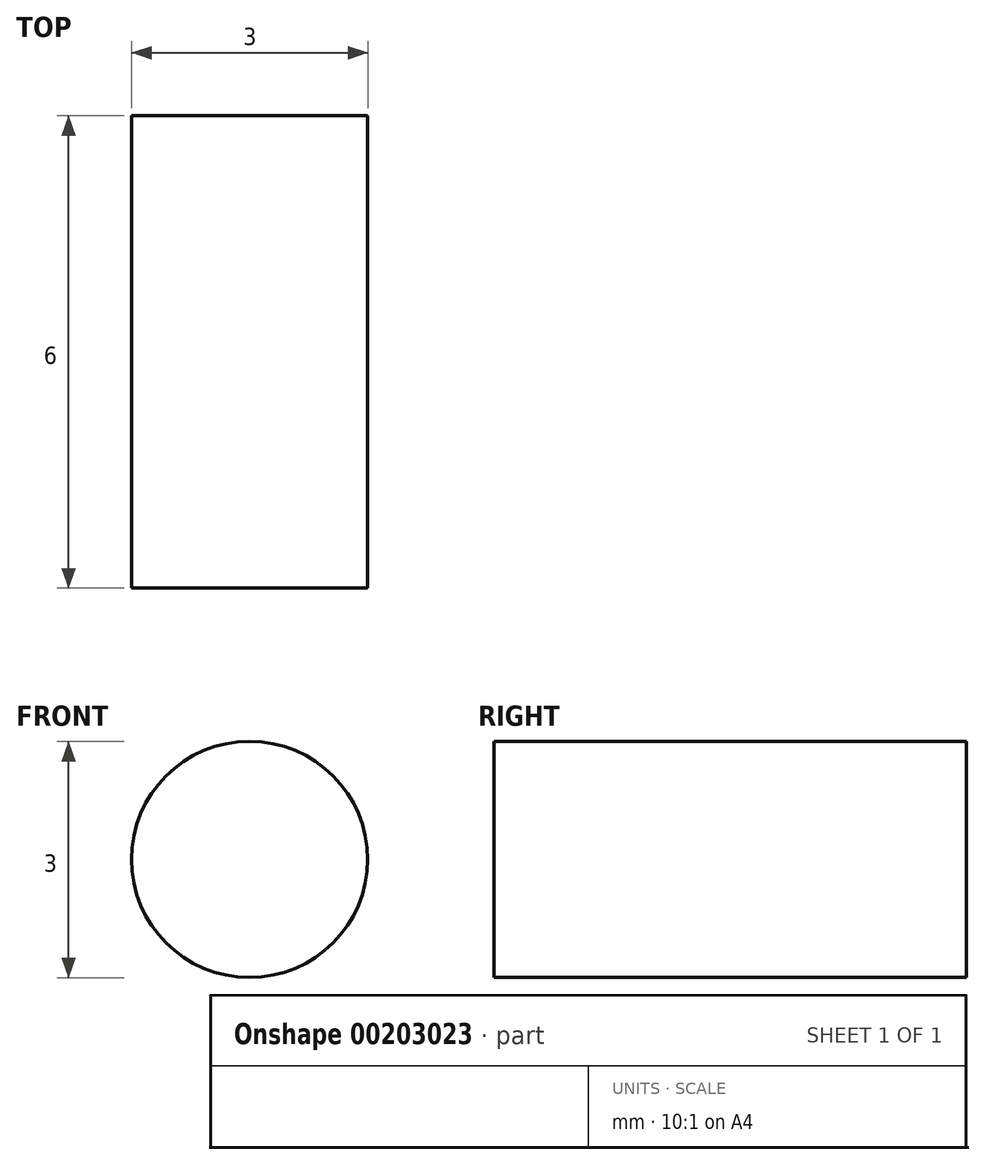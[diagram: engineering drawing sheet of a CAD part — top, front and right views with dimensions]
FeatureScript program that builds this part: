
annotation { "Feature Type Name" : "Feature", "Feature Type Description" : "" }
export const myFeature = defineFeature(function(context is Context, id is Id, definition is map)
    precondition{}
    {
        {
            var Q0;
            Q0=qCreatedBy(makeId("Front.planeOp"),FACE);
            var sketch = newSketch(context, id + "F0", { "sketchPlane" : qUnion([Q0])});
            skCircle(sketch, "E0", {"center": v(110.94, -30.5) * mm, "radius": 1.5 * mm});
            skCircle(sketch, "E1", {"center": v(110.94, 49.1) * mm, "radius": 1.5 * mm});
            skCircle(sketch, "E2", {"center": v(10.94, -30.5) * mm, "radius": 1.5 * mm});
            skCircle(sketch, "E3", {"center": v(10.94, 49.1) * mm, "radius": 1.5 * mm});
            skLineSegment(sketch, "E4", {"start": v(13.94, -37) * mm, "end": v(13.94, -34) * mm});
            skLineSegment(sketch, "E5", {"start": v(13.94, -34) * mm, "end": v(7.94, -34) * mm});
            skLineSegment(sketch, "E6", {"start": v(7.94, -34) * mm, "end": v(7.94, -37) * mm});
            skLineSegment(sketch, "E7", {"start": v(7.94, -37) * mm, "end": v(13.94, -37) * mm});
            skLineSegment(sketch, "E8", {"start": v(13.94, -24) * mm, "end": v(13.94, -27) * mm});
            skLineSegment(sketch, "E9", {"start": v(13.94, -27) * mm, "end": v(7.94, -27) * mm});
            skLineSegment(sketch, "E10", {"start": v(7.94, -27) * mm, "end": v(7.94, -24) * mm});
            skLineSegment(sketch, "E11", {"start": v(7.94, -24) * mm, "end": v(13.94, -24) * mm});
            skLineSegment(sketch, "E12", {"start": v(7.94, 42.6) * mm, "end": v(7.94, 45.6) * mm});
            skLineSegment(sketch, "E13", {"start": v(7.94, 45.6) * mm, "end": v(13.94, 45.6) * mm});
            skLineSegment(sketch, "E14", {"start": v(13.94, 45.6) * mm, "end": v(13.94, 42.6) * mm});
            skLineSegment(sketch, "E15", {"start": v(13.94, 42.6) * mm, "end": v(7.94, 42.6) * mm});
            skLineSegment(sketch, "E16", {"start": v(7.94, 55.6) * mm, "end": v(7.94, 52.6) * mm});
            skLineSegment(sketch, "E17", {"start": v(7.94, 52.6) * mm, "end": v(13.94, 52.6) * mm});
            skLineSegment(sketch, "E18", {"start": v(13.94, 52.6) * mm, "end": v(13.94, 55.6) * mm});
            skLineSegment(sketch, "E19", {"start": v(13.94, 55.6) * mm, "end": v(7.94, 55.6) * mm});
            skLineSegment(sketch, "E20", {"start": v(113.94, 42.6) * mm, "end": v(113.94, 45.6) * mm});
            skLineSegment(sketch, "E21", {"start": v(113.94, 45.6) * mm, "end": v(107.94, 45.6) * mm});
            skLineSegment(sketch, "E22", {"start": v(107.94, 45.6) * mm, "end": v(107.94, 42.6) * mm});
            skLineSegment(sketch, "E23", {"start": v(107.94, 42.6) * mm, "end": v(113.94, 42.6) * mm});
            skLineSegment(sketch, "E24", {"start": v(113.94, 55.6) * mm, "end": v(113.94, 52.6) * mm});
            skLineSegment(sketch, "E25", {"start": v(113.94, 52.6) * mm, "end": v(107.94, 52.6) * mm});
            skLineSegment(sketch, "E26", {"start": v(107.94, 52.6) * mm, "end": v(107.94, 55.6) * mm});
            skLineSegment(sketch, "E27", {"start": v(107.94, 55.6) * mm, "end": v(113.94, 55.6) * mm});
            skLineSegment(sketch, "E28", {"start": v(107.94, -37) * mm, "end": v(107.94, -34) * mm});
            skLineSegment(sketch, "E29", {"start": v(107.94, -34) * mm, "end": v(113.94, -34) * mm});
            skLineSegment(sketch, "E30", {"start": v(113.94, -34) * mm, "end": v(113.94, -37) * mm});
            skLineSegment(sketch, "E31", {"start": v(113.94, -37) * mm, "end": v(107.94, -37) * mm});
            skLineSegment(sketch, "E32", {"start": v(107.94, -24) * mm, "end": v(107.94, -27) * mm});
            skLineSegment(sketch, "E33", {"start": v(107.94, -27) * mm, "end": v(113.94, -27) * mm});
            skLineSegment(sketch, "E34", {"start": v(113.94, -27) * mm, "end": v(113.94, -24) * mm});
            skLineSegment(sketch, "E35", {"start": v(113.94, -24) * mm, "end": v(107.94, -24) * mm});
            skLineSegment(sketch, "E36", {"start": v(83.94, 44.1) * mm, "end": v(83.94, 47.1) * mm});
            skLineSegment(sketch, "E37", {"start": v(83.94, 47.1) * mm, "end": v(77.94, 47.1) * mm});
            skLineSegment(sketch, "E38", {"start": v(77.94, 47.1) * mm, "end": v(77.94, 44.1) * mm});
            skLineSegment(sketch, "E39", {"start": v(77.94, 44.1) * mm, "end": v(83.94, 44.1) * mm});
            skLineSegment(sketch, "E40", {"start": v(37.94, 44.1) * mm, "end": v(37.94, 47.1) * mm});
            skLineSegment(sketch, "E41", {"start": v(37.94, 47.1) * mm, "end": v(43.94, 47.1) * mm});
            skLineSegment(sketch, "E42", {"start": v(43.94, 47.1) * mm, "end": v(43.94, 44.1) * mm});
            skLineSegment(sketch, "E43", {"start": v(43.94, 44.1) * mm, "end": v(37.94, 44.1) * mm});
            skLineSegment(sketch, "E44", {"start": v(30.9, -34.68) * mm, "end": v(29.96, -37.52) * mm});
            skLineSegment(sketch, "E45", {"start": v(29.96, -37.52) * mm, "end": v(35.65, -39.42) * mm});
            skLineSegment(sketch, "E46", {"start": v(35.65, -39.42) * mm, "end": v(36.6, -36.57) * mm});
            skLineSegment(sketch, "E47", {"start": v(36.6, -36.57) * mm, "end": v(30.9, -34.68) * mm});
            skLineSegment(sketch, "E48", {"start": v(90.97, -34.68) * mm, "end": v(91.92, -37.52) * mm});
            skLineSegment(sketch, "E49", {"start": v(91.92, -37.52) * mm, "end": v(86.22, -39.42) * mm});
            skLineSegment(sketch, "E50", {"start": v(86.22, -39.42) * mm, "end": v(85.27, -36.57) * mm});
            skLineSegment(sketch, "E51", {"start": v(85.27, -36.57) * mm, "end": v(90.97, -34.68) * mm});
            skLineSegment(sketch, "E52", {"start": v(57.94, -44.5) * mm, "end": v(57.94, -47.5) * mm});
            skLineSegment(sketch, "E53", {"start": v(57.94, -47.5) * mm, "end": v(63.94, -47.5) * mm});
            skLineSegment(sketch, "E54", {"start": v(63.94, -47.5) * mm, "end": v(63.94, -44.5) * mm});
            skLineSegment(sketch, "E55", {"start": v(63.94, -44.5) * mm, "end": v(57.94, -44.5) * mm});
            skLineSegment(sketch, "E56", {"start": v(83.94, 58.1) * mm, "end": v(83.94, 53.1) * mm});
            skLineSegment(sketch, "E57", {"start": v(83.94, 53.1) * mm, "end": v(80.94, 53.1) * mm});
            skLineSegment(sketch, "E58", {"start": v(80.94, 53.1) * mm, "end": v(77.94, 53.1) * mm});
            skLineSegment(sketch, "E59", {"start": v(77.94, 53.1) * mm, "end": v(77.94, 58.1) * mm});
            skLineSegment(sketch, "E60", {"start": v(77.94, 58.1) * mm, "end": v(76.94, 59.1) * mm});
            skLineSegment(sketch, "E61", {"start": v(76.94, 59.1) * mm, "end": v(44.94, 59.1) * mm});
            skLineSegment(sketch, "E62", {"start": v(44.94, 59.1) * mm, "end": v(43.94, 58.1) * mm});
            skLineSegment(sketch, "E63", {"start": v(43.94, 58.1) * mm, "end": v(43.94, 53.1) * mm});
            skLineSegment(sketch, "E64", {"start": v(43.94, 53.1) * mm, "end": v(40.94, 53.1) * mm});
            skLineSegment(sketch, "E65", {"start": v(40.94, 53.1) * mm, "end": v(37.94, 53.1) * mm});
            skLineSegment(sketch, "E66", {"start": v(37.94, 53.1) * mm, "end": v(37.94, 58.1) * mm});
            skLineSegment(sketch, "E67", {"start": v(37.94, 58.1) * mm, "end": v(36.94, 59.1) * mm});
            skLineSegment(sketch, "E68", {"start": v(36.94, 59.1) * mm, "end": v(5.94, 59.1) * mm});
            skArc(sketch, "E69", {"start": v(5.94, 59.1) * mm, "mid": v(2.4, 57.65) * mm, "end": v(0.94, 54.1) * mm});
            skLineSegment(sketch, "E70", {"start": v(0.94, 54.1) * mm, "end": v(0.94, -36.9) * mm});
            skArc(sketch, "E71", {"start": v(0.94, -36.9) * mm, "mid": v(1.88, -39.82) * mm, "end": v(4.36, -41.64) * mm});
            skLineSegment(sketch, "E72", {"start": v(4.36, -41.64) * mm, "end": v(25.22, -48.59) * mm});
            skLineSegment(sketch, "E73", {"start": v(25.22, -48.59) * mm, "end": v(26.48, -47.96) * mm});
            skLineSegment(sketch, "E74", {"start": v(26.48, -47.96) * mm, "end": v(28.06, -43.21) * mm});
            skLineSegment(sketch, "E75", {"start": v(28.06, -43.21) * mm, "end": v(30.9, -44.16) * mm});
            skLineSegment(sketch, "E76", {"start": v(30.9, -44.16) * mm, "end": v(33.75, -45.11) * mm});
            skLineSegment(sketch, "E77", {"start": v(33.75, -45.11) * mm, "end": v(32.17, -49.85) * mm});
            skLineSegment(sketch, "E78", {"start": v(32.17, -49.85) * mm, "end": v(32.8, -51.12) * mm});
            skLineSegment(sketch, "E79", {"start": v(32.8, -51.12) * mm, "end": v(56.62, -59.06) * mm});
            skArc(sketch, "E80", {"start": v(56.62, -59.06) * mm, "mid": v(57.52, -58.92) * mm, "end": v(57.94, -58.1) * mm});
            skLineSegment(sketch, "E81", {"start": v(57.94, -58.1) * mm, "end": v(57.94, -53.5) * mm});
            skLineSegment(sketch, "E82", {"start": v(57.94, -53.5) * mm, "end": v(60.94, -53.5) * mm});
            skLineSegment(sketch, "E83", {"start": v(60.94, -53.5) * mm, "end": v(63.94, -53.5) * mm});
            skLineSegment(sketch, "E84", {"start": v(63.94, -53.5) * mm, "end": v(63.94, -58.1) * mm});
            skArc(sketch, "E85", {"start": v(63.94, -58.1) * mm, "mid": v(64.35, -58.92) * mm, "end": v(65.25, -59.06) * mm});
            skLineSegment(sketch, "E86", {"start": v(65.25, -59.06) * mm, "end": v(89.07, -51.12) * mm});
            skLineSegment(sketch, "E87", {"start": v(89.07, -51.12) * mm, "end": v(89.7, -49.85) * mm});
            skLineSegment(sketch, "E88", {"start": v(89.7, -49.85) * mm, "end": v(88.12, -45.11) * mm});
            skLineSegment(sketch, "E89", {"start": v(88.12, -45.11) * mm, "end": v(90.97, -44.16) * mm});
            skLineSegment(sketch, "E90", {"start": v(90.97, -44.16) * mm, "end": v(93.81, -43.21) * mm});
            skLineSegment(sketch, "E91", {"start": v(93.81, -43.21) * mm, "end": v(95.4, -47.96) * mm});
            skLineSegment(sketch, "E92", {"start": v(95.4, -47.96) * mm, "end": v(96.66, -48.59) * mm});
            skLineSegment(sketch, "E93", {"start": v(96.66, -48.59) * mm, "end": v(117.52, -41.64) * mm});
            skArc(sketch, "E94", {"start": v(117.52, -41.64) * mm, "mid": v(120, -39.82) * mm, "end": v(120.94, -36.9) * mm});
            skLineSegment(sketch, "E95", {"start": v(120.94, -36.9) * mm, "end": v(120.94, 54.1) * mm});
            skArc(sketch, "E96", {"start": v(120.94, 54.1) * mm, "mid": v(119.47, 57.65) * mm, "end": v(115.94, 59.1) * mm});
            skLineSegment(sketch, "E97", {"start": v(115.94, 59.1) * mm, "end": v(84.94, 59.1) * mm});
            skLineSegment(sketch, "E98", {"start": v(84.94, 59.1) * mm, "end": v(83.94, 58.1) * mm});
            skLineSegment(sketch, "E99", {"start": v(33.68, 31.5) * mm, "end": v(33.68, 37.5) * mm});
            skLineSegment(sketch, "E100", {"start": v(33.68, 37.5) * mm, "end": v(38.68, 37.5) * mm});
            skLineSegment(sketch, "E101", {"start": v(38.68, 37.5) * mm, "end": v(38.68, 31.5) * mm});
            skLineSegment(sketch, "E102", {"start": v(38.68, 31.5) * mm, "end": v(33.68, 31.5) * mm});
            skCircle(sketch, "E103", {"center": v(20.94, -20.5) * mm, "radius": 1.6 * mm});
            skCircle(sketch, "E104", {"center": v(30.94, -20.5) * mm, "radius": 1.6 * mm});
            skCircle(sketch, "E105", {"center": v(90.94, -20.5) * mm, "radius": 1.6 * mm});
            skCircle(sketch, "E106", {"center": v(100.94, -20.5) * mm, "radius": 1.6 * mm});
            skCircle(sketch, "E107", {"center": v(20.94, -10.5) * mm, "radius": 1.6 * mm});
            skCircle(sketch, "E108", {"center": v(30.94, -10.5) * mm, "radius": 1.6 * mm});
            skCircle(sketch, "E109", {"center": v(90.94, -10.5) * mm, "radius": 1.6 * mm});
            skCircle(sketch, "E110", {"center": v(100.94, -10.5) * mm, "radius": 1.6 * mm});
            skCircle(sketch, "E111", {"center": v(20.94, 29.5) * mm, "radius": 1.6 * mm});
            skCircle(sketch, "E112", {"center": v(30.94, 29.5) * mm, "radius": 1.6 * mm});
            skCircle(sketch, "E113", {"center": v(40.94, 29.5) * mm, "radius": 1.6 * mm});
            skCircle(sketch, "E114", {"center": v(50.94, 29.5) * mm, "radius": 1.6 * mm});
            skCircle(sketch, "E115", {"center": v(60.94, 29.5) * mm, "radius": 1.6 * mm});
            skCircle(sketch, "E116", {"center": v(70.94, 29.5) * mm, "radius": 1.6 * mm});
            skCircle(sketch, "E117", {"center": v(80.94, 29.5) * mm, "radius": 1.6 * mm});
            skCircle(sketch, "E118", {"center": v(90.94, 29.5) * mm, "radius": 1.6 * mm});
            skCircle(sketch, "E119", {"center": v(100.94, 29.5) * mm, "radius": 1.6 * mm});
            skCircle(sketch, "E120", {"center": v(20.94, 39.5) * mm, "radius": 1.6 * mm});
            skCircle(sketch, "E121", {"center": v(30.94, 39.5) * mm, "radius": 1.6 * mm});
            skCircle(sketch, "E122", {"center": v(40.94, 39.5) * mm, "radius": 1.6 * mm});
            skCircle(sketch, "E123", {"center": v(50.94, 39.5) * mm, "radius": 1.6 * mm});
            skCircle(sketch, "E124", {"center": v(60.94, 39.5) * mm, "radius": 1.6 * mm});
            skCircle(sketch, "E125", {"center": v(70.94, 39.5) * mm, "radius": 1.6 * mm});
            skCircle(sketch, "E126", {"center": v(80.94, 39.5) * mm, "radius": 1.6 * mm});
            skCircle(sketch, "E127", {"center": v(90.94, 39.5) * mm, "radius": 1.6 * mm});
            skCircle(sketch, "E128", {"center": v(100.94, 39.5) * mm, "radius": 1.6 * mm});
            skCircle(sketch, "E129", {"center": v(70.94, -20.5) * mm, "radius": 1.6 * mm});
            skCircle(sketch, "E130", {"center": v(60.94, -20.5) * mm, "radius": 1.6 * mm});
            skCircle(sketch, "E131", {"center": v(50.94, -20.5) * mm, "radius": 1.6 * mm});
            skLineSegment(sketch, "E132", {"start": v(83.2, 31.5) * mm, "end": v(83.2, 37.5) * mm});
            skLineSegment(sketch, "E133", {"start": v(83.2, 37.5) * mm, "end": v(88.2, 37.5) * mm});
            skLineSegment(sketch, "E134", {"start": v(88.2, 37.5) * mm, "end": v(88.2, 31.5) * mm});
            skLineSegment(sketch, "E135", {"start": v(88.2, 31.5) * mm, "end": v(83.2, 31.5) * mm});
            skLineSegment(sketch, "E136", {"start": v(20.94, 3) * mm, "end": v(20.94, 16) * mm});
            skArc(sketch, "E137", {"start": v(20.94, 16) * mm, "mid": v(22.4, 19.54) * mm, "end": v(25.94, 21) * mm});
            skLineSegment(sketch, "E138", {"start": v(25.94, 21) * mm, "end": v(95.94, 21) * mm});
            skArc(sketch, "E139", {"start": v(95.94, 21) * mm, "mid": v(99.47, 19.54) * mm, "end": v(100.94, 16) * mm});
            skLineSegment(sketch, "E140", {"start": v(100.94, 16) * mm, "end": v(100.94, 3) * mm});
            skArc(sketch, "E141", {"start": v(100.94, 3) * mm, "mid": v(99.47, -0.53) * mm, "end": v(95.94, -2) * mm});
            skLineSegment(sketch, "E142", {"start": v(95.94, -2) * mm, "end": v(25.94, -2) * mm});
            skArc(sketch, "E143", {"start": v(25.94, -2) * mm, "mid": v(22.4, -0.53) * mm, "end": v(20.94, 3) * mm});
            skCircle(sketch, "E144", {"center": v(40.94, -10.5) * mm, "radius": 1.6 * mm});
            skCircle(sketch, "E145", {"center": v(50.94, -10.5) * mm, "radius": 1.6 * mm});
            skCircle(sketch, "E146", {"center": v(60.94, -10.5) * mm, "radius": 1.6 * mm});
            skCircle(sketch, "E147", {"center": v(70.94, -10.5) * mm, "radius": 1.6 * mm});
            skCircle(sketch, "E148", {"center": v(80.94, -20.5) * mm, "radius": 1.6 * mm});
            skCircle(sketch, "E149", {"center": v(80.94, -10.5) * mm, "radius": 1.6 * mm});
            skCircle(sketch, "E150", {"center": v(40.94, -20.5) * mm, "radius": 1.6 * mm});
            skCircle(sketch, "E151", {"center": v(70.94, -30.5) * mm, "radius": 1.6 * mm});
            skCircle(sketch, "E152", {"center": v(60.94, -30.5) * mm, "radius": 1.6 * mm});
            skCircle(sketch, "E153", {"center": v(50.94, -30.5) * mm, "radius": 1.6 * mm});
            skCircle(sketch, "E154", {"center": v(80.94, -30.5) * mm, "radius": 1.6 * mm});
            skCircle(sketch, "E155", {"center": v(40.94, -30.5) * mm, "radius": 1.6 * mm});
            skCircle(sketch, "E156", {"center": v(70.94, -40.5) * mm, "radius": 1.6 * mm});
            skCircle(sketch, "E157", {"center": v(60.94, -40.5) * mm, "radius": 1.6 * mm});
            skCircle(sketch, "E158", {"center": v(50.94, -40.5) * mm, "radius": 1.6 * mm});
            skSolve(sketch);
        }
        {
            var Q0;
            Q0=makeQuery(id+"F0.imprint","IMPRINT",FACE,{"disambiguationData":[TD([[makeQuery(id+"F0.imprint","IMPRINT",EDGE,{"derivedFrom":sQuery(id+"F0.wireOp",EDGE,"E0")}),1.0]])]});
            extrude(context, id + "F1", {"entities" : qUnion([Q0]), "depth" : 6 * mm});
        }
    });
